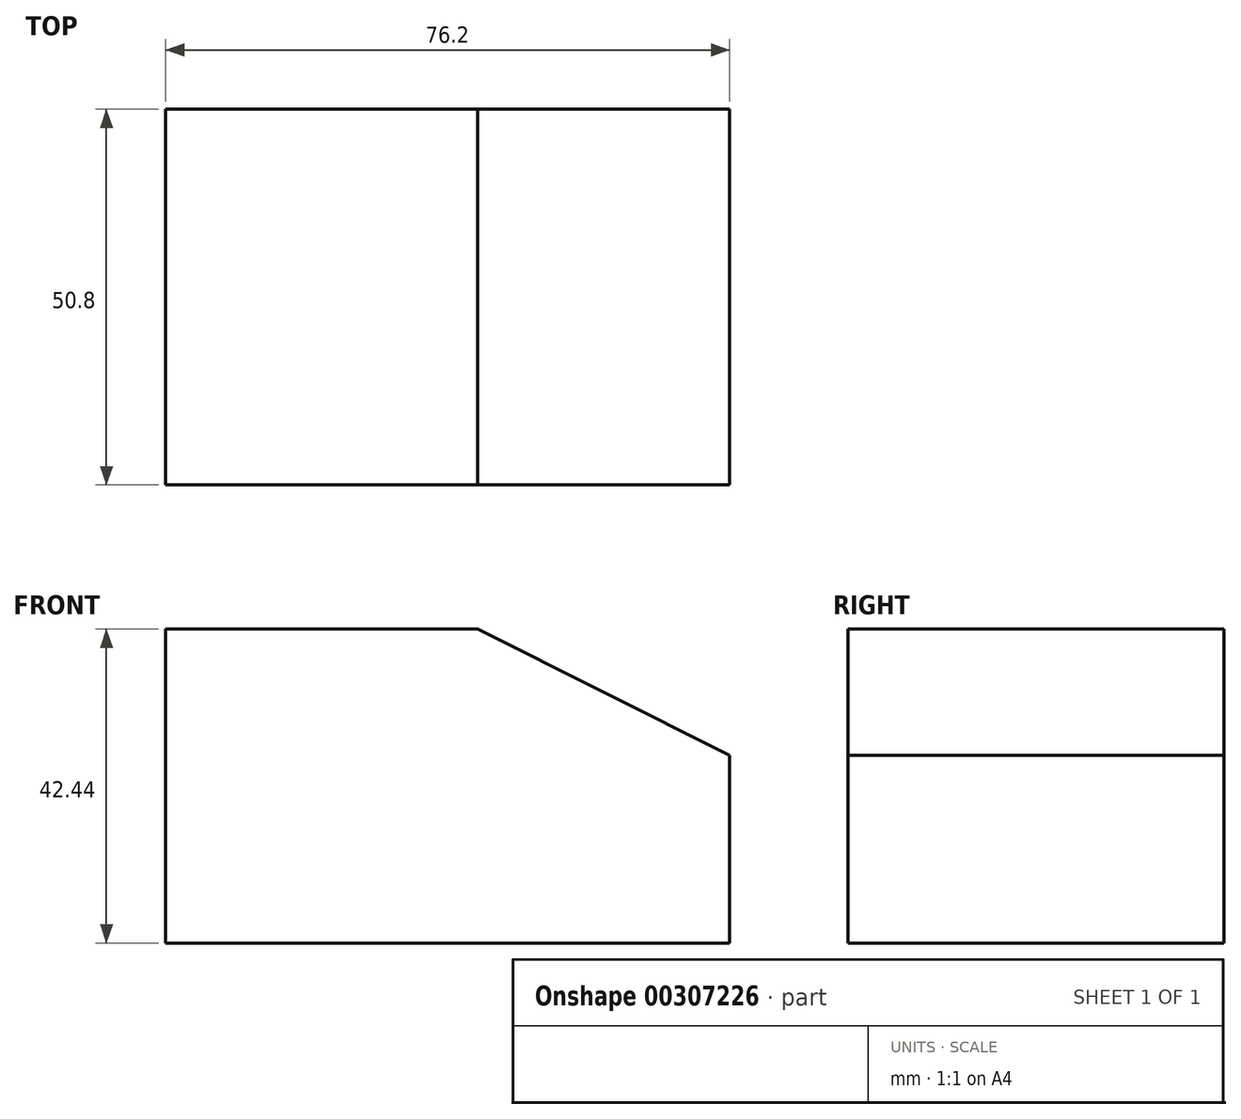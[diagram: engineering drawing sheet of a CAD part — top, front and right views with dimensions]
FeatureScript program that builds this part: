
annotation { "Feature Type Name" : "Feature", "Feature Type Description" : "" }
export const myFeature = defineFeature(function(context is Context, id is Id, definition is map)
    precondition{}
    {
        {
            var Q0;
            Q0=qCreatedBy(makeId("Front.planeOp"),FACE);
            var sketch = newSketch(context, id + "F0", { "sketchPlane" : qUnion([Q0])});
            skLineSegment(sketch, "E0", {"start": v(-35.26, -50.3) * mm, "end": v(40.94, -50.3) * mm});
            skLineSegment(sketch, "E1", {"start": v(40.94, -50.3) * mm, "end": v(40.94, -24.9) * mm});
            skLineSegment(sketch, "E2", {"start": v(40.94, -24.9) * mm, "end": v(6.86, -7.85) * mm});
            skLineSegment(sketch, "E3", {"start": v(6.86, -7.85) * mm, "end": v(-35.26, -7.85) * mm});
            skLineSegment(sketch, "E4", {"start": v(-35.26, -7.85) * mm, "end": v(-35.26, -50.3) * mm});
            skSolve(sketch);
        }
        {
            var Q0;
            Q0=makeQuery(id+"F0.imprint","IMPRINT",FACE,{"disambiguationData":[TD([[makeQuery(id+"F0.imprint","IMPRINT",EDGE,{"derivedFrom":sQuery(id+"F0.wireOp",EDGE,"E0")}),1.0]])]});
            extrude(context, id + "F1", {"entities" : qUnion([Q0]), "depth" : 50.8 * mm});
        }
    });
